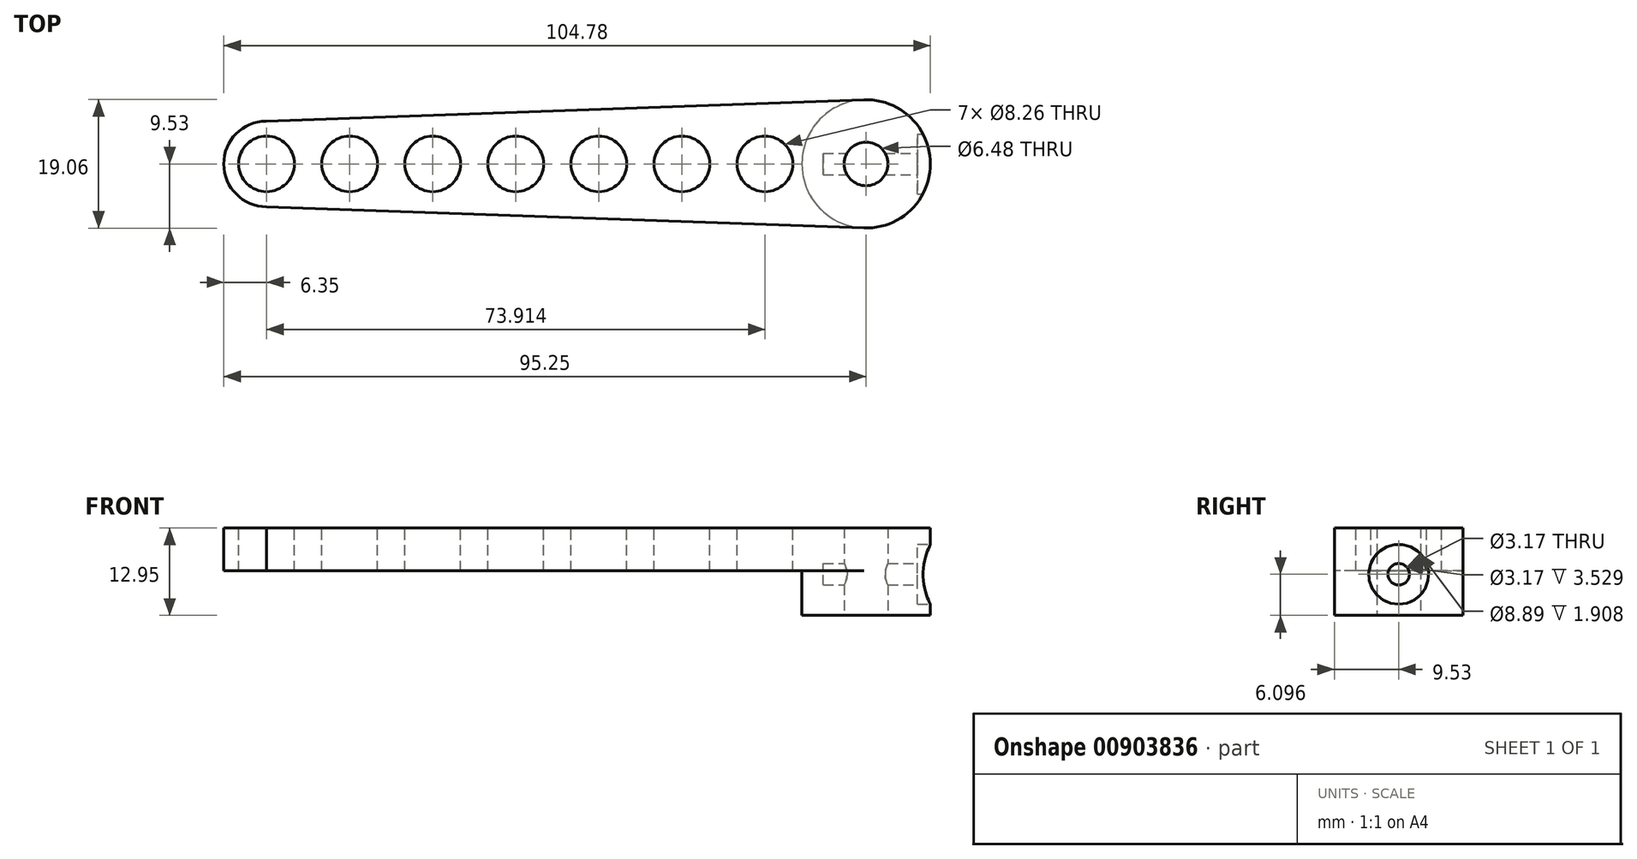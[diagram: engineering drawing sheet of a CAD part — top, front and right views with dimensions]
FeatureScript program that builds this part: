
annotation { "Feature Type Name" : "Feature", "Feature Type Description" : "" }
export const myFeature = defineFeature(function(context is Context, id is Id, definition is map)
    precondition{}
    {
        {
            var Q0;
            Q0=qCreatedBy(makeId("Top.planeOp"),FACE);
            var sketch = newSketch(context, id + "F0", { "sketchPlane" : qUnion([Q0])});
            skCircle(sketch, "E0", {"center": v(0, 0) * mm, "radius": 3.24 * mm});
            skCircle(sketch, "E1", {"center": v(0, 0) * mm, "radius": 9.53 * mm});
            skSolve(sketch);
        }
        {
            var Q0;
            Q0=makeQuery(id+"F0.imprint","IMPRINT",FACE,{"disambiguationData":[TD([[makeQuery(id+"F0.imprint","IMPRINT",EDGE,{"derivedFrom":sQuery(id+"F0.wireOp",EDGE,"E0")}),-1.0]])]});
            extrude(context, id + "F1", {"entities" : qUnion([Q0]), "depth" : 12.95 * mm, "offsetDistance" : 25.4 * mm});
        }
        {
            var Q0;
            Q0=makeQuery(id+"F1.opExtrude","CAP_FACE",FACE,{"disambiguationData":[OSD([sQuery(id+"F0.wireOp",EDGE,"E0"),sQuery(id+"F0.wireOp",EDGE,"E1")])],"isStart":false});
            var sketch = newSketch(context, id + "F2", { "sketchPlane" : qUnion([Q0])});
            skCircle(sketch, "E2", {"center": v(0, 0) * mm, "radius": 9.53 * mm});
            skCircle(sketch, "E3", {"center": v(-88.9, 0) * mm, "radius": 6.35 * mm});
            skLineSegment(sketch, "E4", {"start": v(-88.97, 6.35) * mm, "end": v(0, 9.53) * mm});
            skLineSegment(sketch, "E5", {"start": v(-88.9, -6.35) * mm, "end": v(0, -9.53) * mm});
            skCircle(sketch, "E6", {"center": v(-88.9, 0) * mm, "radius": 4.13 * mm});
            skCircle(sketch, "E7.1.0.0", {"center": v(-76.58, 0) * mm, "radius": 4.13 * mm});
            skCircle(sketch, "E7.2.0.0", {"center": v(-64.26, 0) * mm, "radius": 4.13 * mm});
            skCircle(sketch, "E7.3.0.0", {"center": v(-51.94, 0) * mm, "radius": 4.13 * mm});
            skCircle(sketch, "E7.4.0.0", {"center": v(-39.62, 0) * mm, "radius": 4.13 * mm});
            skLineSegment(sketch, "E7.direction1", {"start": v(-88.9, 0) * mm, "end": v(-76.58, 0) * mm, "construction": true});
            skCircle(sketch, "E8.0.5.0", {"center": v(-27.3, 0) * mm, "radius": 4.13 * mm});
            skCircle(sketch, "E9.0.6.0", {"center": v(-14.99, 0) * mm, "radius": 4.13 * mm});
            skSolve(sketch);
        }
        {
            var Q0;
            Q0=qSketchRegion(id+"F2",true);
            extrude(context, id + "F3", {"entities" : qUnion([Q0]), "operationType" : NewBodyOperationType.ADD, "oppositeDirection" : true, "depth" : 6.35 * mm, "offsetDistance" : 25.4 * mm});
        }
        {
            var Q0;
            Q0=qCreatedBy(makeId("Right.planeOp"),FACE);
            cPlane(context, id + "F4", {"entities" : qUnion([Q0]), "cplaneType" : CPlaneType.OFFSET, "offset" : 25.4 * mm, "width" : 152.4 * mm, "height" : 152.4 * mm});
        }
        {
            var Q0;
            Q0=qCreatedBy(id+"F4.planeOp",FACE);
            var sketch = newSketch(context, id + "F5", { "sketchPlane" : qUnion([Q0])});
            skLineSegment(sketch, "E10", {"start": v(0, 0) * mm, "end": v(0, 6.1) * mm, "construction": true});
            skCircle(sketch, "E11", {"center": v(0, 6.1) * mm, "radius": 1.59 * mm});
            skCircle(sketch, "E12", {"center": v(0, 6.1) * mm, "radius": 4.45 * mm});
            skSolve(sketch);
        }
        {
            var Q0;
            Q0=makeQuery(id+"F5.imprint","IMPRINT",FACE,{"disambiguationData":[TD([[makeQuery(id+"F5.imprint","IMPRINT",EDGE,{"derivedFrom":sQuery(id+"F5.wireOp",EDGE,"E11")}),1.0]])]});
            extrude(context, id + "F6", {"entities" : qUnion([Q0]), "operationType" : NewBodyOperationType.REMOVE, "oppositeDirection" : true, "depth" : 31.75 * mm, "offsetDistance" : 25.4 * mm});
        }
        {
            var Q0;
            Q0=makeQuery(id+"F0.imprint","IMPRINT",FACE,{"disambiguationData":[TD([[makeQuery(id+"F0.imprint","IMPRINT",EDGE,{"derivedFrom":sQuery(id+"F0.wireOp",EDGE,"E0")}),1.0]])]});
            extrude(context, id + "F7", {"entities" : qUnion([Q0]), "operationType" : NewBodyOperationType.REMOVE, "depth" : 25.4 * mm, "offsetDistance" : 25.4 * mm});
        }
        {
            var Q0;
            Q0=makeQuery(id+"F5.imprint","IMPRINT",FACE,{"disambiguationData":[TD([[makeQuery(id+"F5.imprint","IMPRINT",EDGE,{"derivedFrom":sQuery(id+"F5.wireOp",EDGE,"E11")}),-1.0]])]});
            extrude(context, id + "F8", {"entities" : qUnion([Q0]), "operationType" : NewBodyOperationType.REMOVE, "oppositeDirection" : true, "depth" : 17.78 * mm, "offsetDistance" : 25.4 * mm});
        }
    });
